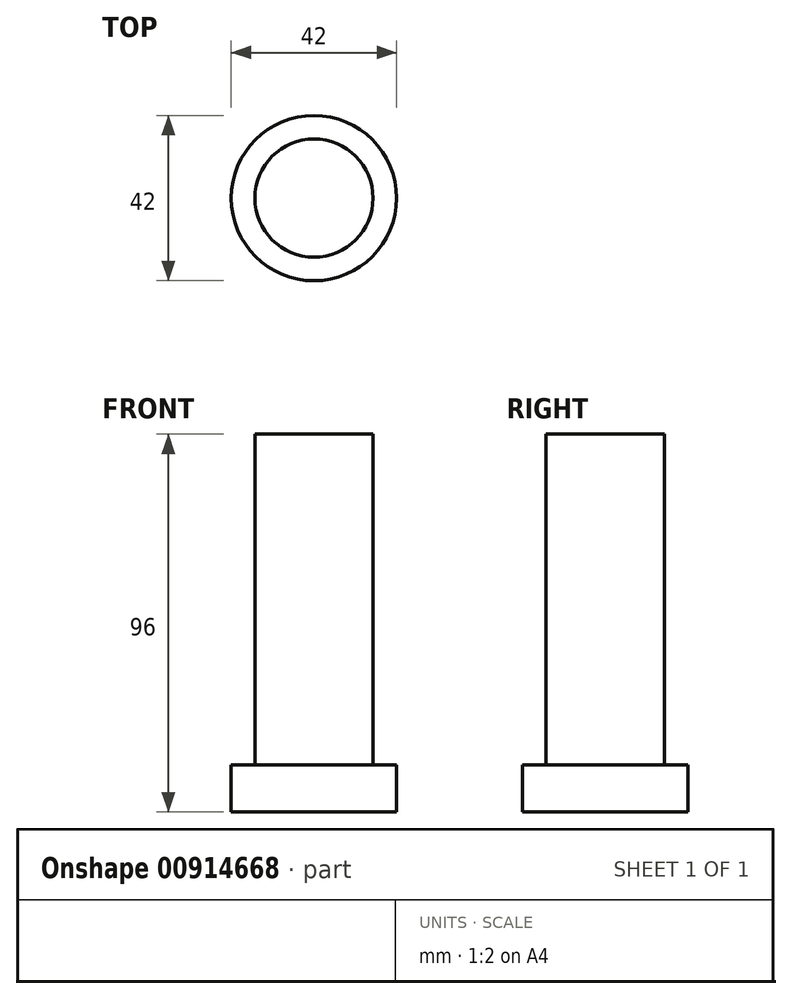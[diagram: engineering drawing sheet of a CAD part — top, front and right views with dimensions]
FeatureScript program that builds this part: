
annotation { "Feature Type Name" : "Feature", "Feature Type Description" : "" }
export const myFeature = defineFeature(function(context is Context, id is Id, definition is map)
    precondition{}
    {
        {
            var Q0;
            Q0=qCreatedBy(makeId("Top.planeOp"),FACE);
            var sketch = newSketch(context, id + "F0", { "sketchPlane" : qUnion([Q0])});
            skPoint(sketch, "E0", {"position": v(0, 0) * mm});
            skCircle(sketch, "E1", {"center": v(0, 0) * mm, "radius": 21 * mm});
            skSolve(sketch);
        }
        {
            var Q0;
            Q0=makeQuery(id+"F0.imprint","IMPRINT",FACE,{"disambiguationData":[TD([[makeQuery(id+"F0.imprint","IMPRINT",EDGE,{"derivedFrom":sQuery(id+"F0.wireOp",EDGE,"E1")}),1.0]])]});
            extrude(context, id + "F1", {"entities" : qUnion([Q0]), "depth" : 12 * mm, "offsetDistance" : 25 * mm});
        }
        {
            var Q0;
            Q0=makeQuery(id+"F1.opExtrude","CAP_FACE",FACE,{"disambiguationData":[OSD([sQuery(id+"F0.wireOp",EDGE,"E1")])],"isStart":false});
            var sketch = newSketch(context, id + "F2", { "sketchPlane" : qUnion([Q0])});
            skCircle(sketch, "E2", {"center": v(0, 0) * mm, "radius": 15 * mm});
            skSolve(sketch);
        }
        {
            var Q0;
            Q0=makeQuery(id+"F2.imprint","IMPRINT",FACE,{"disambiguationData":[TD([[makeQuery(id+"F2.imprint","IMPRINT",EDGE,{"derivedFrom":sQuery(id+"F2.wireOp",EDGE,"E2")}),1.0]])]});
            extrude(context, id + "F3", {"entities" : qUnion([Q0]), "operationType" : NewBodyOperationType.ADD, "depth" : 84 * mm, "offsetDistance" : 25 * mm});
        }
    });
